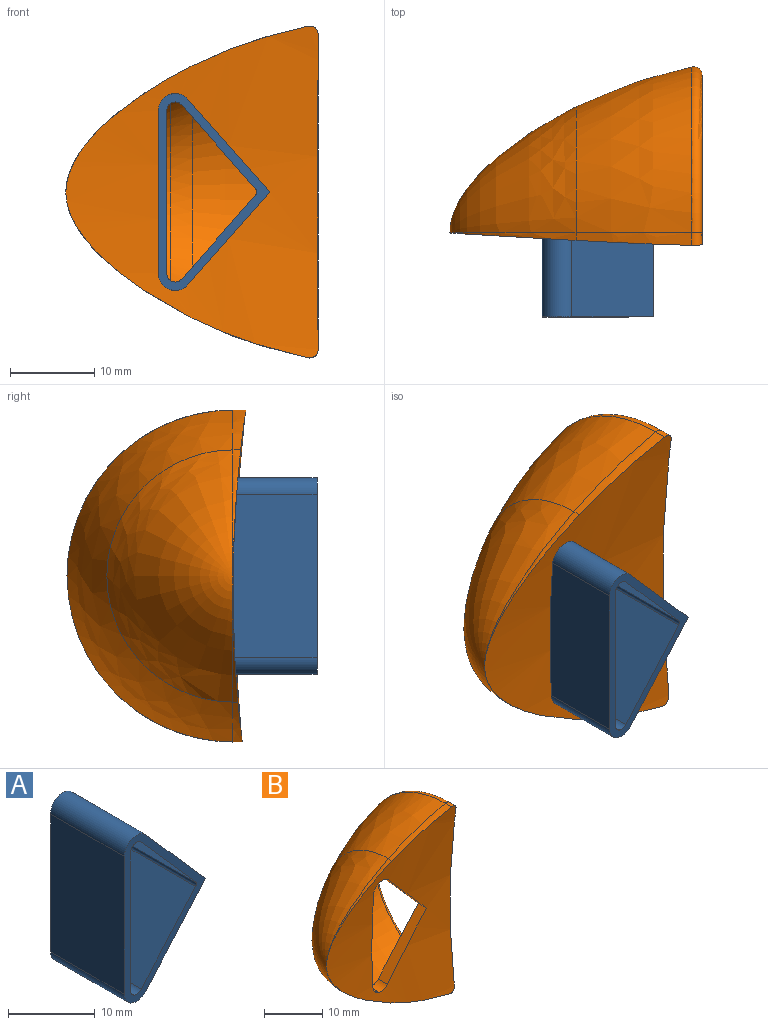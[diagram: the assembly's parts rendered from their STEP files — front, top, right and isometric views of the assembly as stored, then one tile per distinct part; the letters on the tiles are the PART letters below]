
ASSEMBLY  parts=2 mates=1
PART A: 19 faces, bbox 14.6x12x25.3 mm
  f0: plane 12x11.03mm, normal (0.75,0,0.66), area 176.5mm2, adj f1,f10,f11,f12,f13
  f1: cylinder r=2mm len=12mm, axis (0,1,0), area 58.1mm2, adj f0,f2,f11,f14
  f2: plane 19.42x12mm, normal (-1,0,0), area 233mm2, adj f1,f3,f11,f16
  f3: cylinder r=2mm len=12mm, axis (0,1,0), area 58.1mm2, adj f2,f10,f11,f18
  f4: cylinder r=0.5mm len=11mm, axis (0,1,0), area 8mm2, adj f5,f9,f11,f15
  f5: plane 11x10.04mm, normal (-0.75,0,0.66), area 147.2mm2, adj f4,f6,f11,f17
  f6: cylinder r=1mm len=11mm, axis (0,1,0), area 26.6mm2, adj f5,f7,f11,f18
  f7: plane 19.42x11mm, normal (1,0,0), area 213.6mm2, adj f6,f8,f11,f16
  f8: cylinder r=1mm len=11mm, axis (0,1,0), area 26.6mm2, adj f7,f9,f11,f14
  f9: plane 11x10.04mm, normal (-0.75,0,-0.66), area 147.2mm2, adj f4,f8,f11,f13
  f10: plane 12x11.03mm, normal (0.75,0,-0.66), area 176.5mm2, adj f0,f3,f11,f12,f17
  f11: plane 23.42x13.23mm, normal (0,-1,0), area 55.2mm2, adj f0,f1,f2,f3,f4,f5,f6,f7
  f12: plane 1.98x0.88mm, normal (0,1,0), area 0.4mm2, adj f0,f10,f15
  f13: cylinder r=1mm len=10.7mm, axis (0.66,0,-0.75), area 21mm2, adj f0,f9,f14,f15
  f14: torus R=2mm, axis (0,-1,0), area 5.2mm2, adj f1,f8,f13,f16
  f15: torus R=1.5mm, axis (0,-1,0), area 2mm2, adj f4,f12,f13,f17
  f16: cylinder r=1mm len=19.42mm, axis (0,0,1), area 30.5mm2, adj f2,f7,f14,f18
  f17: cylinder r=1mm len=10.7mm, axis (-0.66,0,-0.75), area 21mm2, adj f5,f10,f15,f18
  f18: torus R=2mm, axis (0,-1,0), area 5.2mm2, adj f3,f6,f16,f17
PART B: 23 faces, bbox 30.8x23.7x43.6 mm
  f0: extruded ~14.79x13.38mm, area 4.9mm2, adj f5,f16,f22
  f1: revolved ~26x13mm, area 100.9mm2, adj f2,f7,f8,f9,f10
  f2: revolved ~35.55x16.89mm, area 682.6mm2, adj f1,f8,f17,f21
  f3: plane 3.07x0.39mm, normal (1,0,0), area 0.6mm2, adj f18,f21,f22
  f4: revolved ~39.44x19.72mm, area 809.5mm2, adj f5,f13,f16,f19
  f5: revolved ~30x15mm, area 593.1mm2, adj f0,f4,f14,f15
  f6: plane 19.42x10.14mm, normal (1,0,0), area 150.3mm2, adj f7,f9,f10,f22
  f7: torus R=9.71mm, axis (1,0,0), area 88.5mm2, adj f1,f6,f9,f10
  f8: plane 35.17x14.94mm, normal (0,1,0), area 274mm2, adj f1,f2,f9,f10,f11,f12,f21
  f9: cylinder r=2mm len=3.5mm, axis (0,-1,0), area 6.4mm2, adj f1,f6,f7,f8,f11,f22
  f10: cylinder r=2mm len=3.5mm, axis (0,-1,0), area 5.3mm2, adj f1,f6,f7,f8,f12,f22
  f11: plane 11.04x9.74mm, normal (-0.75,0,-0.66), area 32.4mm2, adj f8,f9,f12,f22
  f12: plane 11.04x9.73mm, normal (-0.75,0,0.66), area 30.7mm2, adj f8,f10,f11,f22
  f13: extruded ~13.77x4.72mm, area 18.2mm2, adj f4,f14,f18,f22
  f14: extruded ~15x15mm, area 9mm2, adj f5,f13,f15,f22
  f15: extruded ~1.62x0.21mm, area 0mm2, adj f5,f14,f22
  f16: extruded ~13.77x4.72mm, area 12.6mm2, adj f0,f4,f20,f22
  f17: torus R=18.79mm, axis (1,0,0), area 74.7mm2, adj f2,f19,f21
  f18: cylinder r=1mm len=1.53mm, axis (0,1,0), area 2.4mm2, adj f3,f13,f19,f21,f22
  f19: torus R=18.74mm, axis (1,0,0), area 108.7mm2, adj f4,f17,f18,f20
  f20: cylinder r=1mm len=1.23mm, axis (0,1,0), area 1.7mm2, adj f16,f19,f21,f22
  f21: bspline ~41.24x3mm, area 151.5mm2, adj f2,f3,f8,f17,f18,f20,f22
  f22: cylinder r=150mm len=39.49mm, axis (-1,0,0), area 636.5mm2, adj f0,f3,f6,f9,f10,f11,f12,f13
PLACE A t=(26.7,68.96,-54.15)mm
PLACE B t=(-6.52,-83.04,-15.53)mm
MATE fastened A.f12 <-> B.f8  axis (0,1,0) through (-2.29,68.96,-13.91)mm
